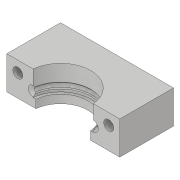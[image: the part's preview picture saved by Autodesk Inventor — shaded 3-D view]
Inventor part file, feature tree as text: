
AUTODESK INVENTOR PART (.ipt)
format: ipt  version: 2020 (Build 240168000, 168)  size: 280,576 bytes
history: native  units: in
note: dims shown in document units (in); Inventor stores cm internally (conversion verified against a paired STEP export)
features: sketch x21, extrude x11, sweep x5, chamfer x2, plane x1, mirror x1
ambient origin geometry x8: Origin, YZ Plane, XZ Plane, XY Plane, X Axis, Y Axis, Z Axis, Center Point
bodies: Solid1 (feature_tree)
feature tree (41):
  extrude  "Extrusion1"  Depth=1.6142in
  extrude  "Extrusion2"  Depth=0.7874in
  extrude  "Extrusion3"  Depth=0.9252in
  extrude  "Extrusion4"  Depth=0.1772in TaperAngle=0.0deg
  extrude  "Extrusion5"  Depth=0.1417in
  extrude  "Extrusion6"  [1 undecoded]
  plane  "Work Plane1"
  mirror  "Mirror1"
  sweep  "Sweep1"
  sweep  "Sweep2"
  extrude  "Extrusion7"  Depth=0.8628in
  extrude  "Extrusion8"  Depth=0.063in
  extrude  "Extrusion9"  TaperAngle=0.0deg  [1 undecoded]
  sketch  "Sketch16"  dims[d39=0.1181in d40=0.0in d41=0.0in]
  sketch  "Sketch17"  dims[d42=0.3937in d43=0.0in d44=0.0394in d45=0.0787in d46=45.0deg]
  sweep  "Sweep3"
  sweep  "Sweep4"
  extrude  "Extrusion10"  Depth=0.0394in TaperAngle=45.0deg
  sweep  "Sweep5"
  extrude  "Extrusion11"  [1 undecoded]
  chamfer  "Chamfer1"  [1 undecoded]
  chamfer  "Chamfer2"  [1 undecoded]
  sketch  "Sketch1"  dims[d0=1.6142in d1=1.6142in]
  sketch  "Sketch3"  dims[d2=0.374in d3=0.0in d5=0.7874in]
  sketch  "Sketch4"  dims[d6=0.3937in d7=0.0in d8=0.9252in]
  sketch  "Sketch5"  dims[d9=0.1969in d10=0.0in d11=0.1772in d12=0.0in]
  sketch  "Sketch6"  dims[d13=0.8071in d14=0.0in d15=0.1417in]
  sketch  "Sketch8"  dims[d16=0.8071in d17=0.0in d18=-0.8071in]
  sketch  "Sketch9"  dims[d19=0.0in d20=0.0in d21=0.063in]
  sketch  "Sketch11"  dims[d22=0.0in d23=0.0in d24=0.0787in d25=0.0in]
  sketch  "Sketch12"  dims[d26=0.0276in d27=0.0in d28=0.8628in]
  sketch  "3D Sketch1"
  sketch  "Sketch13"  dims[d29=0.5906in d30=0.0in d31=0.063in]
  sketch  "Sketch14"  dims[d32=0.0in d33=0.0in d34=0.0in d35=0.0in]
  sketch  "Sketch15"  dims[d36=0.0118in d37=0.0in d38=0.0394in]
  sketch  "3D Sketch2"
  sketch  "Sketch18"  dims[d47=0.0118in d48=0.0787in d49=45.0deg]
  sketch  "3D Sketch3"
  sketch  "Sketch19"
  sketch  "Sketch20"
  sketch  "Sketch21"
note: 5 required parameter values undecoded (feature->parameter linkage not recoverable at this tier; creation-order binding heuristic only, values carry confidence <= 0.55)
